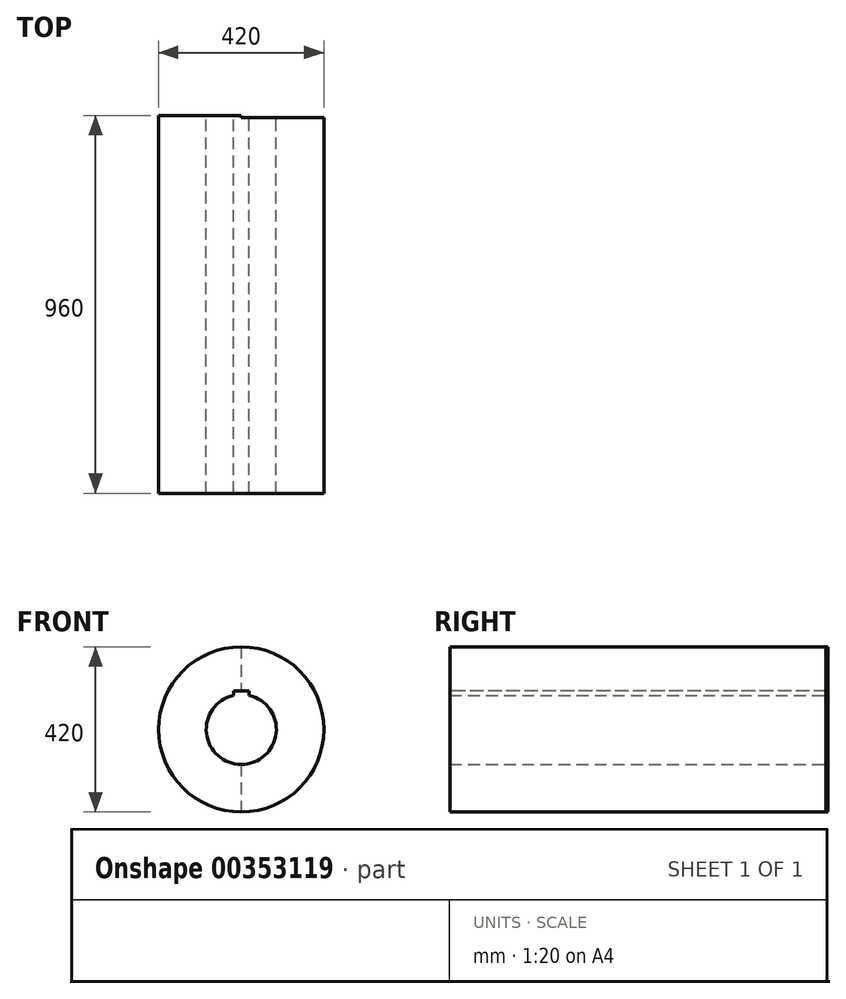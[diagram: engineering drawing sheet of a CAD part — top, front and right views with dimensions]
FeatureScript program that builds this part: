
annotation { "Feature Type Name" : "Feature", "Feature Type Description" : "" }
export const myFeature = defineFeature(function(context is Context, id is Id, definition is map)
    precondition{}
    {
        {
            var Q0;
            Q0=qCreatedBy(makeId("Front.planeOp"),FACE);
            var sketch = newSketch(context, id + "F0", { "sketchPlane" : qUnion([Q0])});
            skCircle(sketch, "E0", {"center": v(0, 0) * mm, "radius": 210 * mm});
            skSolve(sketch);
        }
        {
            var Q0;
            Q0=makeQuery(id+"F0.imprint","IMPRINT",FACE,{"disambiguationData":[TD([[makeQuery(id+"F0.imprint","IMPRINT",EDGE,{"derivedFrom":sQuery(id+"F0.wireOp",EDGE,"E0")}),1.0]])]});
            var sketch = newSketch(context, id + "F1", { "sketchPlane" : qUnion([Q0])});
            skCircle(sketch, "E1", {"center": v(0, 0) * mm, "radius": 89 * mm});
            skSolve(sketch);
        }
        {
            var Q0;
            Q0=makeQuery(id+"F1.imprint","IMPRINT",FACE,{"disambiguationData":[TD([[makeQuery(id+"F1.imprint","IMPRINT",EDGE,{"derivedFrom":sQuery(id+"F1.wireOp",EDGE,"E1")}),-1.0]])]});
            extrude(context, id + "F2", {"entities" : qUnion([Q0]), "depth" : 960 * mm});
        }
        {
            var Q0;
            Q0=makeQuery(id+"F2.opExtrude","CAP_FACE",FACE,{"disambiguationData":[OSD([sQuery(id+"F0.wireOp",EDGE,"E0"),sQuery(id+"F1.wireOp",EDGE,"E1")])],"isStart":false});
            var sketch = newSketch(context, id + "F3", { "sketchPlane" : qUnion([Q0])});
            skLineSegment(sketch, "E2.bottom", {"start": v(-20, 98) * mm, "end": v(20, 98) * mm});
            skLineSegment(sketch, "E2.top", {"start": v(-20, 62.03) * mm, "end": v(20, 62.03) * mm});
            skLineSegment(sketch, "E2.left", {"start": v(-20, 98) * mm, "end": v(-20, 62.03) * mm});
            skLineSegment(sketch, "E2.right", {"start": v(20, 98) * mm, "end": v(20, 62.03) * mm});
            skPoint(sketch, "E2.middle", {"position": v(0, 80.02) * mm});
            skLineSegment(sketch, "E3", {"start": v(0, 0) * mm, "end": v(0, -89) * mm});
            skSolve(sketch);
        }
        {
            var Q0;
            Q0 = qSketchRegion(id + "F3", true);
            extrude(context, id + "F4", {"entities" : qUnion([Q0]), "operationType" : NewBodyOperationType.REMOVE, "oppositeDirection" : true, "depth" : 1035 * mm});
        }
        {
            var Q0;
            Q0=makeQuery(id+"F0.imprint","IMPRINT",FACE,{"disambiguationData":[TD([[makeQuery(id+"F0.imprint","IMPRINT",EDGE,{"derivedFrom":sQuery(id+"F0.wireOp",EDGE,"E0")}),1.0]])]});
            var sketch = newSketch(context, id + "F5", { "sketchPlane" : qUnion([Q0])});
            skLineSegment(sketch, "E4", {"start": v(0, 0) * mm, "end": v(0, -241.78) * mm});
            skLineSegment(sketch, "E5", {"start": v(0, -241.78) * mm, "end": v(256, -190.36) * mm});
            skLineSegment(sketch, "E6", {"start": v(256, -190.36) * mm, "end": v(264.75, 22.97) * mm});
            skLineSegment(sketch, "E7", {"start": v(264.75, 22.97) * mm, "end": v(219.9, 219.9) * mm});
            skLineSegment(sketch, "E8", {"start": v(219.9, 219.9) * mm, "end": v(88.61, 269.13) * mm});
            skLineSegment(sketch, "E9", {"start": v(88.61, 269.13) * mm, "end": v(0, 269.13) * mm});
            skLineSegment(sketch, "E10", {"start": v(0, 269.13) * mm, "end": v(0, 0) * mm});
            skSolve(sketch);
        }
        {
            var Q0;
            Q0 = qSketchRegion(id + "F5", true);
            extrude(context, id + "F6", {"entities" : qUnion([Q0]), "operationType" : NewBodyOperationType.REMOVE, "depth" : 5 * mm});
        }
    });
